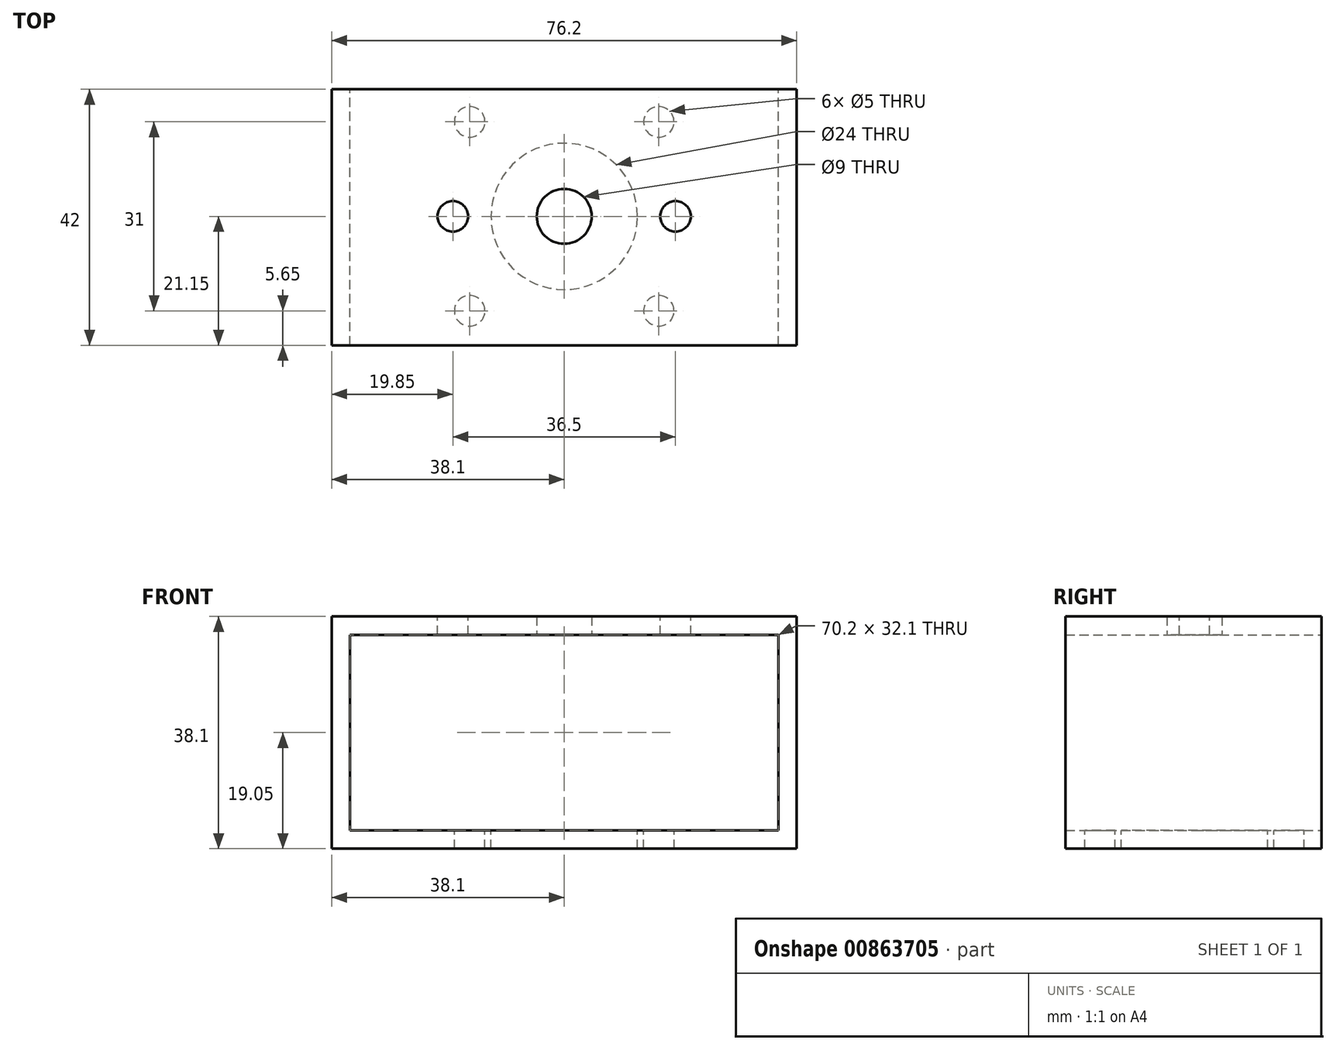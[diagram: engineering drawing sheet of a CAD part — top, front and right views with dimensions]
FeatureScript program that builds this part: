
annotation { "Feature Type Name" : "Feature", "Feature Type Description" : "" }
export const myFeature = defineFeature(function(context is Context, id is Id, definition is map)
    precondition{}
    {
        {
            var Q0;
            Q0=qCreatedBy(makeId("Front.planeOp"),FACE);
            var sketch = newSketch(context, id + "F0", { "sketchPlane" : qUnion([Q0])});
            skLineSegment(sketch, "E0.bottom", {"start": v(0, 0) * mm, "end": v(76.2, 0) * mm});
            skLineSegment(sketch, "E0.top", {"start": v(0, 38.1) * mm, "end": v(76.2, 38.1) * mm});
            skLineSegment(sketch, "E0.left", {"start": v(0, 0) * mm, "end": v(0, 38.1) * mm});
            skLineSegment(sketch, "E0.right", {"start": v(76.2, 0) * mm, "end": v(76.2, 38.1) * mm});
            skLineSegment(sketch, "E1.0", {"start": v(3, 35.1) * mm, "end": v(73.2, 35.1) * mm});
            skLineSegment(sketch, "E1.1", {"start": v(3, 3) * mm, "end": v(3, 35.1) * mm});
            skLineSegment(sketch, "E1.2", {"start": v(3, 3) * mm, "end": v(73.2, 3) * mm});
            skLineSegment(sketch, "E1.3", {"start": v(73.2, 3) * mm, "end": v(73.2, 35.1) * mm});
            skSolve(sketch);
        }
        {
            var Q0;
            Q0 = qSketchRegion(id + "F0", true);
            extrude(context, id + "F1", {"entities" : qUnion([Q0]), "depth" : 42 * mm, "offsetDistance" : 25 * mm});
        }
        {
            var Q0;
            Q0=makeQuery(id+"F1.opExtrude","SWEPT_FACE",FACE,{"disambiguationData":[OSD([sQuery(id+"F0.wireOp",EDGE,"E1.2")])]});
            var sketch = newSketch(context, id + "F2", { "sketchPlane" : qUnion([Q0])});
            skCircle(sketch, "E2", {"center": v(53.6, -5.35) * mm, "radius": 2.5 * mm});
            skCircle(sketch, "E3", {"center": v(53.6, -36.35) * mm, "radius": 2.5 * mm});
            skCircle(sketch, "E4", {"center": v(22.6, -36.35) * mm, "radius": 2.5 * mm});
            skCircle(sketch, "E5", {"center": v(22.6, -5.35) * mm, "radius": 2.5 * mm});
            skCircle(sketch, "E6", {"center": v(38.1, -20.85) * mm, "radius": 12 * mm});
            skSolve(sketch);
        }
        {
            var Q0;
            Q0 = qSketchRegion(id + "F2", true);
            extrude(context, id + "F3", {"entities" : qUnion([Q0]), "operationType" : NewBodyOperationType.REMOVE, "oppositeDirection" : true, "depth" : 5 * mm, "offsetDistance" : 25 * mm});
        }
        {
            var Q0;
            Q0=makeQuery(id+"F1.opExtrude","SWEPT_FACE",FACE,{"disambiguationData":[OSD([sQuery(id+"F0.wireOp",EDGE,"E1.0")])]});
            var sketch = newSketch(context, id + "F4", { "sketchPlane" : qUnion([Q0])});
            skCircle(sketch, "E7", {"center": v(38.1, 20.85) * mm, "radius": 4.5 * mm});
            skSolve(sketch);
        }
        {
            var Q0;
            Q0 = qSketchRegion(id + "F4", true);
            extrude(context, id + "F5", {"entities" : qUnion([Q0]), "operationType" : NewBodyOperationType.REMOVE, "oppositeDirection" : true, "depth" : 5 * mm, "offsetDistance" : 25 * mm});
        }
        {
            var Q0;
            Q0=makeQuery(id+"F1.opExtrude","SWEPT_FACE",FACE,{"disambiguationData":[OSD([sQuery(id+"F0.wireOp",EDGE,"E0.top")])]});
            var sketch = newSketch(context, id + "F6", { "sketchPlane" : qUnion([Q0])});
            skPoint(sketch, "E8", {"position": v(19.85, -20.85) * mm});
            skPoint(sketch, "E9", {"position": v(56.35, -20.85) * mm});
            skSolve(sketch);
        }
        {
            var Q0;
            Q0=sQuery(id+"F6.wireOp",VERTEX,"E8");
            var Q1;
            Q1=sQuery(id+"F6.wireOp",VERTEX,"E9");
            var Q2;
            Q2=makeQuery(id+"F1.opExtrude","SWEPT_BODY",BODY,{"disambiguationData":[OSD([sQuery(id+"F0.wireOp",EDGE,"E0.bottom"),sQuery(id+"F0.wireOp",EDGE,"E0.top"),sQuery(id+"F0.wireOp",EDGE,"E0.left"),sQuery(id+"F0.wireOp",EDGE,"E0.right"),sQuery(id+"F0.wireOp",EDGE,"E1.0"),sQuery(id+"F0.wireOp",EDGE,"E1.1"),sQuery(id+"F0.wireOp",EDGE,"E1.2"),sQuery(id+"F0.wireOp",EDGE,"E1.3")])]});
            hole(context, id + "F7", {"style" : HoleStyle.SIMPLE, "endStyle" : HoleEndStyle.BLIND, "holeDiameter" : 5 * mm, "majorDiameter" : 5 * mm, "holeDepth" : 10 * mm, "isTappedThrough" : true, "tappedDepth" : 12 * mm, "tapClearance" : 3, "locations" : qUnion([Q0, Q1]), "scope" : qUnion([Q2])});
        }
    });
